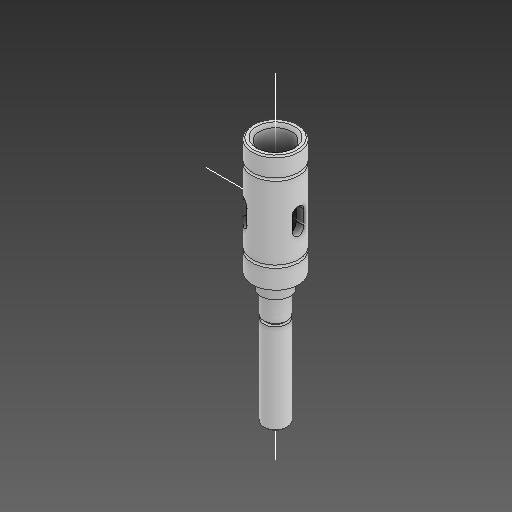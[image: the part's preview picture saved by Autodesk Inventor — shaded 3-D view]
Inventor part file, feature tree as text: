
AUTODESK INVENTOR PART (.ipt)
format: ipt  version: 2021 (Build 250183000, 183)  size: 216,064 bytes
history: native  units: in
note: dims shown in document units (in); Inventor stores cm internally (conversion verified against a paired STEP export)
features: sketch x9, other x8, plane x3
ambient origin geometry x8: Origin, YZ Plane, XZ Plane, XY Plane, X Axis, Y Axis, Z Axis, Center Point
bodies: Solid1 (feature_tree)
feature tree (20):
  other  "iner_sleeve.ipt"
  other  "Solid1::iner_sleeve.ipt"
  other  "TaggingFeature1"
  sketch  "Sketch1"  dims[d0=0.3937in]
  sketch  "Sketch2"
  sketch  "Sketch3"
  sketch  "Sketch5"
  sketch  "Sketch6"
  sketch  "Sketch7"
  sketch  "Sketch8"
  sketch  "Sketch10"
  sketch  "Sketch11"
  plane  "Work Plane1"
  plane  "Work Plane2"
  plane  "Work Plane3"
  other  "Work Axis1"
  other  "Work Axis2"
  other  "Work Axis3"
  other  "Srf1"
  other  "Srf1::Derived"
